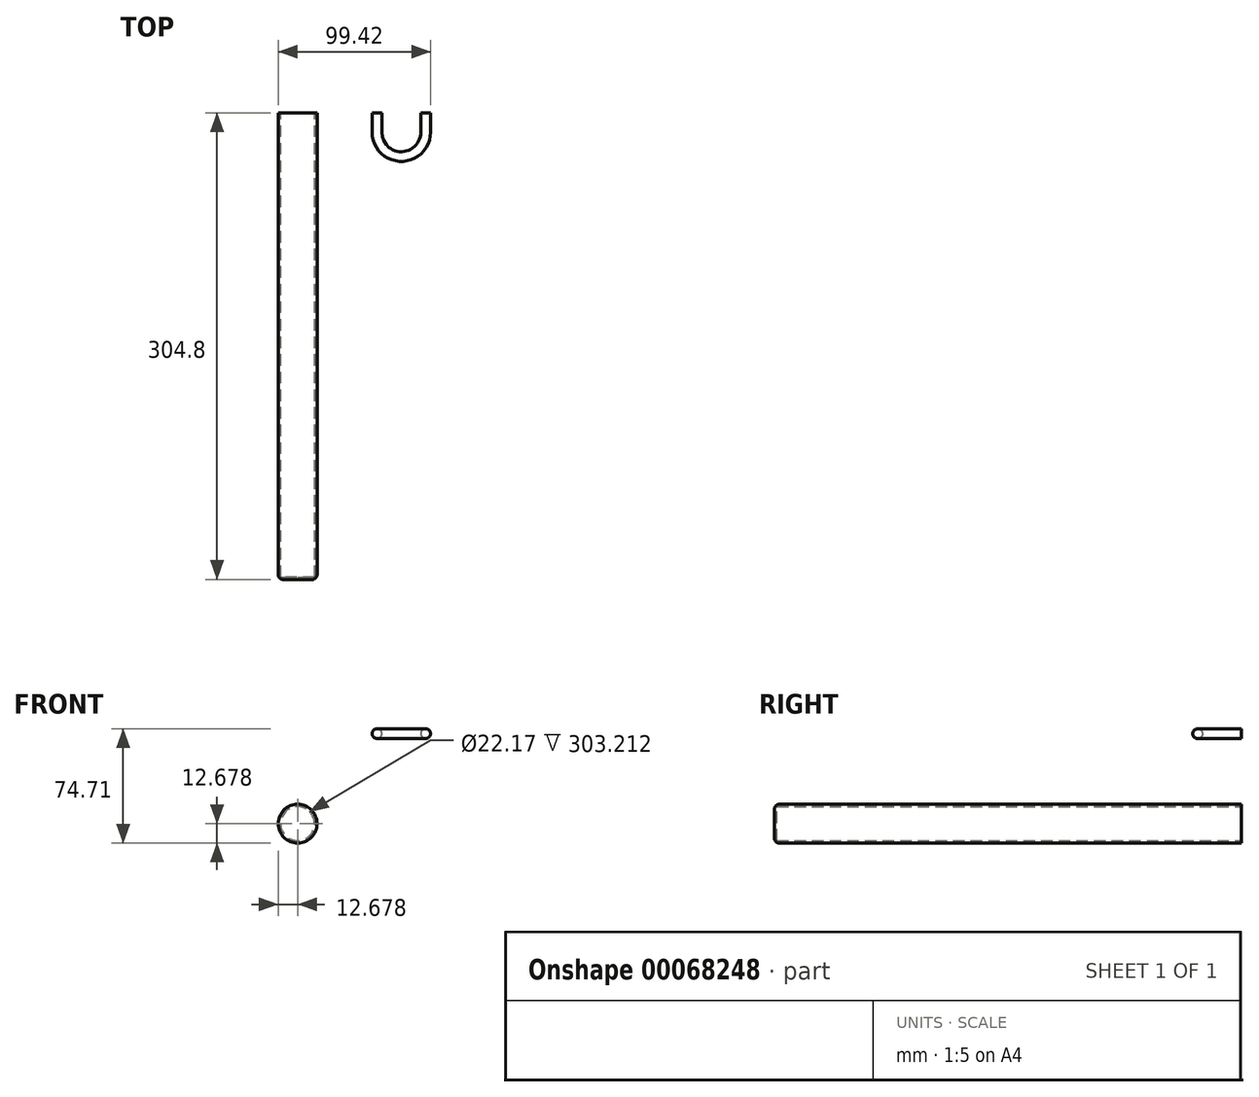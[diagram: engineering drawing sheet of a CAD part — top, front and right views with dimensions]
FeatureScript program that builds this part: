
annotation { "Feature Type Name" : "Feature", "Feature Type Description" : "" }
export const myFeature = defineFeature(function(context is Context, id is Id, definition is map)
    precondition{}
    {
        {
            var Q0;
            Q0=qCreatedBy(makeId("Front.planeOp"),FACE);
            var sketch = newSketch(context, id + "F0", { "sketchPlane" : qUnion([Q0])});
            skCircle(sketch, "E0", {"center": v(0, 0) * mm, "radius": 3.18 * mm});
            skSolve(sketch);
        }
        {
            var Q0;
            Q0=qCreatedBy(makeId("Top.planeOp"),FACE);
            var sketch = newSketch(context, id + "F1", { "sketchPlane" : qUnion([Q0])});
            skLineSegment(sketch, "E1", {"start": v(0, 0) * mm, "end": v(0, -12.7) * mm});
            skLineSegment(sketch, "E2", {"start": v(31.75, 0) * mm, "end": v(31.75, -12.7) * mm});
            skArc(sketch, "E3", {"start": v(0, -12.7) * mm, "mid": v(15.88, -28.57) * mm, "end": v(31.75, -12.7) * mm});
            skSolve(sketch);
        }
        {
            var Q0;
            Q0=makeQuery(id+"F0.imprint","IMPRINT",FACE,{"disambiguationData":[TD([[makeQuery(id+"F0.imprint","IMPRINT",EDGE,{"derivedFrom":sQuery(id+"F0.wireOp",EDGE,"E0")}),1.0]])]});
            var Q1;
            Q1=sQuery(id+"F1.wireOp",EDGE,"E1");
            var Q2;
            Q2=sQuery(id+"F1.wireOp",EDGE,"E3");
            var Q3;
            Q3=sQuery(id+"F1.wireOp",EDGE,"E2");
            sweep(context, id + "F2", {"profiles" : qUnion([Q0]), "path" : qUnion([Q1, Q2, Q3])});
        }
        {
            var Q0;
            Q0=qCreatedBy(makeId("Front.planeOp"),FACE);
            var sketch = newSketch(context, id + "F3", { "sketchPlane" : qUnion([Q0])});
            skCircle(sketch, "E4", {"center": v(-51.81, -58.85) * mm, "radius": 12.67 * mm});
            skSolve(sketch);
        }
        {
            var Q0;
            Q0=makeQuery(id+"F3.imprint","IMPRINT",FACE,{"disambiguationData":[TD([[makeQuery(id+"F3.imprint","IMPRINT",EDGE,{"derivedFrom":sQuery(id+"F3.wireOp",EDGE,"E4")}),1.0]])]});
            extrude(context, id + "F4", {"entities" : qUnion([Q0]), "depth" : 304.8 * mm});
        }
        {
            var Q0;
            Q0=makeQuery(id+"F4.opExtrude","CAP_FACE",FACE,{"disambiguationData":[OSD([sQuery(id+"F3.wireOp",EDGE,"E4")])],"isStart":true});
            shell(context, id + "F5", {"entities" : qUnion([Q0]), "thickness" : 1.59 * mm});
        }
        {
            var Q0;
            Q0=makeQuery(id+"F4.opExtrude","CAP_EDGE",EDGE,{"disambiguationData":[OSD([sQuery(id+"F3.wireOp",EDGE,"E4")])],"isStart":false});
            fillet(context, id + "F6", {"entities" : qUnion([Q0]), "radius" : 3.17 * mm, "tangentPropagation" : true, "allowEdgeOverflow" : false});
        }
    });
